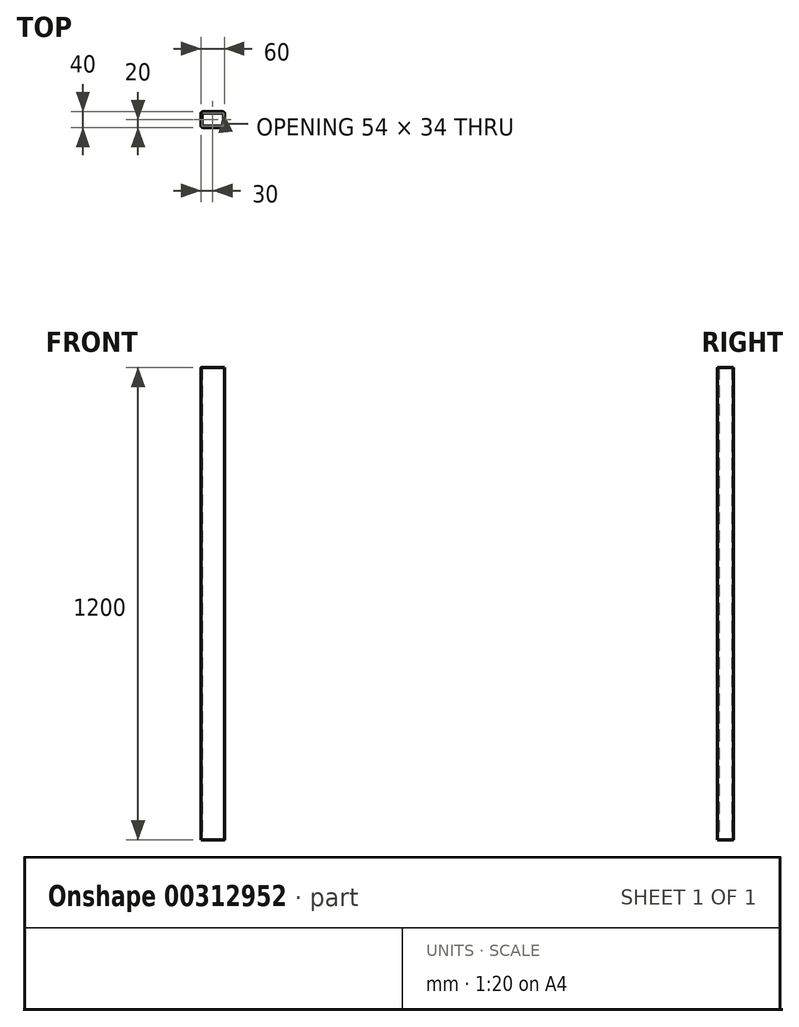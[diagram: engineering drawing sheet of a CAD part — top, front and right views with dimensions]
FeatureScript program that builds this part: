
annotation { "Feature Type Name" : "Feature", "Feature Type Description" : "" }
export const myFeature = defineFeature(function(context is Context, id is Id, definition is map)
    precondition{}
    {
        {
            var Q0;
            Q0=qCreatedBy(makeId("Top.planeOp"),FACE);
            var sketch = newSketch(context, id + "F0", { "sketchPlane" : qUnion([Q0])});
            skLineSegment(sketch, "E0.bottom", {"start": v(25, 20) * mm, "end": v(-25, 20) * mm});
            skLineSegment(sketch, "E0.top", {"start": v(25, -20) * mm, "end": v(-25, -20) * mm});
            skLineSegment(sketch, "E0.left", {"start": v(30, 15) * mm, "end": v(30, -15) * mm});
            skLineSegment(sketch, "E0.right", {"start": v(-30, 15) * mm, "end": v(-30, -15) * mm});
            skPoint(sketch, "E0.middle", {"position": v(0, 0) * mm});
            skLineSegment(sketch, "E1.0", {"start": v(25, 17) * mm, "end": v(-25, 17) * mm});
            skLineSegment(sketch, "E2.0", {"start": v(27, 15) * mm, "end": v(27, -15) * mm});
            skLineSegment(sketch, "E3.0", {"start": v(25, -17) * mm, "end": v(-25, -17) * mm});
            skLineSegment(sketch, "E4.0", {"start": v(-27, 15) * mm, "end": v(-27, -15) * mm});
            skPoint(sketch, "E5.visualSharp", {"position": v(-30, 20) * mm});
            skArc(sketch, "E5.filletArc", {"start": v(-25, 20) * mm, "mid": v(-28.54, 18.54) * mm, "end": v(-30, 15) * mm});
            skPoint(sketch, "E6.visualSharp", {"position": v(30, 20) * mm});
            skArc(sketch, "E6.filletArc", {"start": v(30, 15) * mm, "mid": v(28.54, 18.54) * mm, "end": v(25, 20) * mm});
            skPoint(sketch, "E7.visualSharp", {"position": v(30, -20) * mm});
            skArc(sketch, "E7.filletArc", {"start": v(25, -20) * mm, "mid": v(28.54, -18.54) * mm, "end": v(30, -15) * mm});
            skPoint(sketch, "E8.visualSharp", {"position": v(-30, -20) * mm});
            skArc(sketch, "E8.filletArc", {"start": v(-30, -15) * mm, "mid": v(-28.54, -18.54) * mm, "end": v(-25, -20) * mm});
            skPoint(sketch, "E9.visualSharp", {"position": v(-27, 17) * mm});
            skArc(sketch, "E9.filletArc", {"start": v(-25, 17) * mm, "mid": v(-26.41, 16.41) * mm, "end": v(-27, 15) * mm});
            skPoint(sketch, "E10.visualSharp", {"position": v(27, 17) * mm});
            skArc(sketch, "E10.filletArc", {"start": v(27, 15) * mm, "mid": v(26.41, 16.41) * mm, "end": v(25, 17) * mm});
            skPoint(sketch, "E11.visualSharp", {"position": v(27, -17) * mm});
            skArc(sketch, "E11.filletArc", {"start": v(25, -17) * mm, "mid": v(26.41, -16.41) * mm, "end": v(27, -15) * mm});
            skPoint(sketch, "E12.visualSharp", {"position": v(-27, -17) * mm});
            skArc(sketch, "E12.filletArc", {"start": v(-27, -15) * mm, "mid": v(-26.41, -16.41) * mm, "end": v(-25, -17) * mm});
            skSolve(sketch);
        }
        {
            var Q0;
            Q0=qSketchRegion(id+"F0",true);
            extrude(context, id + "F1", {"entities" : qUnion([Q0]), "depth" : 1200 * mm, "offsetDistance" : 25 * mm});
        }
    });
